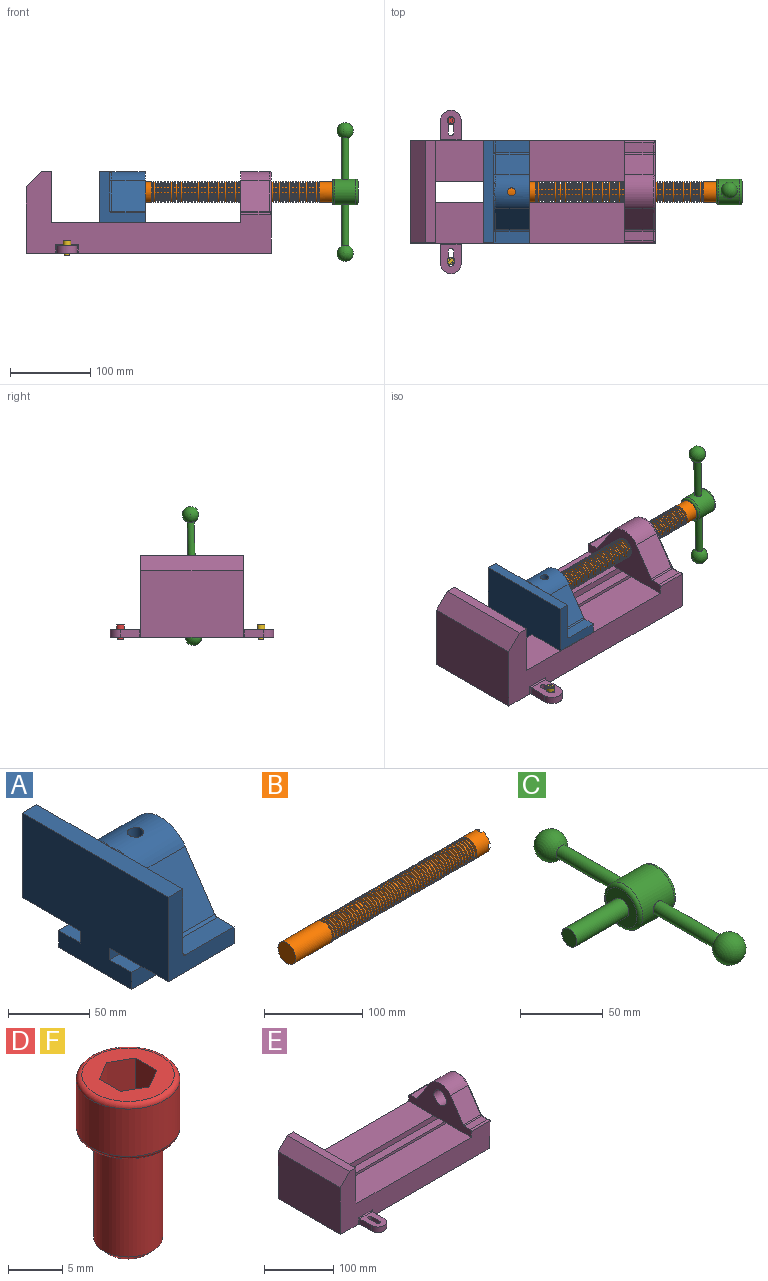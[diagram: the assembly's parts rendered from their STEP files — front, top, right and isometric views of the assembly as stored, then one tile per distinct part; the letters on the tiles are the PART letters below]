
ASSEMBLY  parts=6 mates=6
PART A: 36 faces, bbox 57.2x127x89 mm
  f0: plane 57.15x50.8mm, normal (0,0,-1), area 2903.2mm2, adj f6,f9,f10,f23
  f1: cylinder r=12.7mm len=44.45mm, axis (1,0,0), area 3464.3mm2, adj f6,f15,f16
  f2: plane 41.91x14.52mm, normal (0,0,1), area 608.5mm2, adj f6,f11,f24,f25
  f3: plane 51.86x48.26mm, normal (1,0,0), area 1495.7mm2, adj f8,f10,f31,f33,f35
  f4: plane 51.86x48.26mm, normal (1,0,0), area 1495.7mm2, adj f8,f11,f24,f28,f29
  f5: plane 57.15x50.8mm, normal (0,0,-1), area 2903.2mm2, adj f6,f9,f11,f22
  f6: plane 127x85.09mm, normal (1,0,0), area 5190.6mm2, adj f0,f1,f2,f5,f7,f10,f11,f12
  f7: plane 41.91x14.52mm, normal (0,0,1), area 608.5mm2, adj f6,f10,f30,f31
  f8: plane 127x12.7mm, normal (0,0,1), area 1612.9mm2, adj f3,f4,f9,f10,f11,f26,f34
  f9: plane 127x85.09mm, normal (-1,0,0), area 9096.8mm2, adj f0,f5,f8,f10,f11,f17,f18,f19
  f10: plane 63.5x57.15mm, normal (0,-1,0), area 1372.3mm2, adj f0,f3,f6,f7,f8,f9,f31
  f11: plane 63.5x57.15mm, normal (0,1,0), area 1372.3mm2, adj f2,f4,f5,f6,f8,f9,f24
  f12: plane 41.91x38.43mm, normal (0,-0.83,0.56), area 1939.2mm2, adj f6,f13,f30,f33
  f13: cylinder r=25.4mm len=44.45mm, axis (1,0,0), area 2026.5mm2, adj f6,f12,f14,f16,f26,f28,f34,f35
  f14: plane 41.91x38.43mm, normal (0,0.83,0.56), area 1939.2mm2, adj f6,f13,f25,f29
  f15: plane 25.4x25.4mm, normal (1,0,0), area 506.7mm2, adj f1
  f16: cylinder r=5.08mm len=13.76mm, axis (0,0,1), area 414mm2, adj f1,f13
  f17: plane 57.15x19.05mm, normal (0,0,1), area 1088.7mm2, adj f6,f9,f18,f23
  f18: plane 57.15x12.7mm, normal (0,-1,0), area 725.8mm2, adj f6,f9,f17,f19
  f19: plane 63.5x57.15mm, normal (0,0,-1), area 3629mm2, adj f6,f9,f18,f20
  f20: plane 57.15x12.7mm, normal (0,1,0), area 725.8mm2, adj f6,f9,f19,f21
  f21: plane 57.15x19.05mm, normal (0,0,1), area 1088.7mm2, adj f6,f9,f20,f22
  f22: plane 57.15x8.89mm, normal (0,1,0), area 508.1mm2, adj f5,f6,f9,f21
  f23: plane 57.15x8.89mm, normal (0,-1,0), area 508.1mm2, adj f0,f6,f9,f17
  f24: cylinder r=2.54mm len=14.52mm, axis (0,-1,0), area 57.9mm2, adj f2,f4,f11,f27
  f25: cylinder r=2.54mm len=41.91mm, axis (1,0,0), area 104.3mm2, adj f2,f6,f14,f27
  f26: bspline ~12.24x2.8mm, area 20.9mm2, adj f8,f13,f28
  f27: sphere r=2.54mm, area 6.3mm2, adj f24,f25,f29
  f28: torus R=27.94mm, axis (1,0,0), area 57.8mm2, adj f4,f13,f26,f29
  f29: cylinder r=2.54mm len=39.84mm, axis (0,-0.56,0.83), area 184.6mm2, adj f4,f14,f27,f28
  f30: cylinder r=2.54mm len=41.91mm, axis (1,0,0), area 104.3mm2, adj f6,f7,f12,f32
  f31: cylinder r=2.54mm len=14.52mm, axis (0,-1,0), area 57.9mm2, adj f3,f7,f10,f32
  f32: sphere r=2.54mm, area 6.3mm2, adj f30,f31,f33
  f33: cylinder r=2.54mm len=39.84mm, axis (0,-0.56,-0.83), area 184.6mm2, adj f3,f12,f32,f35
  f34: bspline ~12.24x2.8mm, area 20.9mm2, adj f8,f13,f35
  f35: torus R=27.94mm, axis (1,0,0), area 57.8mm2, adj f3,f13,f33,f34
PART B: 220 faces, bbox 279.4x25.4x25.4 mm
  f0: cylinder r=12.7mm len=25.4mm, axis (-1,0,0), area 1468.2mm2, adj f1,f2,f3,f5,f7,f208,f209,f210
  f1: plane 9.9x9.9mm, normal (1,0,0), area 62.3mm2, adj f0,f4,f213,f216
  f2: plane 9.9x9.9mm, normal (1,0,0), area 62.3mm2, adj f0,f4,f210,f218
  f3: plane 9.9x9.9mm, normal (1,0,0), area 62.3mm2, adj f0,f4,f209,f212
  f4: cylinder r=6.35mm len=25.4mm, axis (1,0,0), area 960.3mm2, adj f1,f2,f3,f5,f6,f208,f209,f210
  f5: plane 9.9x9.9mm, normal (1,0,0), area 62.3mm2, adj f0,f4,f215,f217
  f6: plane 12.7x12.7mm, normal (1,0,0), area 126.7mm2, adj f4
  f7: cone r=12.7mm half-angle=76deg, axis (1,0,0), area 188mm2, adj f0,f9
  f8: cone r=10.16mm half-angle=76deg, axis (-1,0,0), area 188mm2, adj f9,f10
  f9: cylinder r=10.16mm len=20.32mm, axis (1,0,0), area 81.1mm2, adj f7,f8
  f10: cylinder r=12.7mm len=25.4mm, axis (-1,0,0), area 131.7mm2, adj f8,f11
  f11: cone r=12.7mm half-angle=76deg, axis (1,0,0), area 188mm2, adj f10,f13
  f12: cone r=10.16mm half-angle=76deg, axis (-1,0,0), area 188mm2, adj f13,f14
  f13: cylinder r=10.16mm len=20.32mm, axis (1,0,0), area 81.1mm2, adj f11,f12
  f14: cylinder r=12.7mm len=25.4mm, axis (-1,0,0), area 131.7mm2, adj f12,f15
  f15: cone r=12.7mm half-angle=76deg, axis (1,0,0), area 188mm2, adj f14,f17
  f16: cone r=10.16mm half-angle=76deg, axis (-1,0,0), area 188mm2, adj f17,f18
  f17: cylinder r=10.16mm len=20.32mm, axis (1,0,0), area 81.1mm2, adj f15,f16
  f18: cylinder r=12.7mm len=25.4mm, axis (-1,0,0), area 131.7mm2, adj f16,f19
  f19: cone r=12.7mm half-angle=76deg, axis (1,0,0), area 188mm2, adj f18,f21
  f20: cone r=10.16mm half-angle=76deg, axis (-1,0,0), area 188mm2, adj f21,f22
  f21: cylinder r=10.16mm len=20.32mm, axis (1,0,0), area 81.1mm2, adj f19,f20
  f22: cylinder r=12.7mm len=25.4mm, axis (-1,0,0), area 131.7mm2, adj f20,f23
  f23: cone r=12.7mm half-angle=76deg, axis (1,0,0), area 188mm2, adj f22,f25
  f24: cone r=10.16mm half-angle=76deg, axis (-1,0,0), area 188mm2, adj f25,f26
  f25: cylinder r=10.16mm len=20.32mm, axis (1,0,0), area 81.1mm2, adj f23,f24
  f26: cylinder r=12.7mm len=25.4mm, axis (-1,0,0), area 131.7mm2, adj f24,f27
  f27: cone r=12.7mm half-angle=76deg, axis (1,0,0), area 188mm2, adj f26,f29
  f28: cone r=10.16mm half-angle=76deg, axis (-1,0,0), area 188mm2, adj f29,f30
  f29: cylinder r=10.16mm len=20.32mm, axis (1,0,0), area 81.1mm2, adj f27,f28
  f30: cylinder r=12.7mm len=25.4mm, axis (-1,0,0), area 131.7mm2, adj f28,f31
  f31: cone r=12.7mm half-angle=76deg, axis (1,0,0), area 188mm2, adj f30,f33
  f32: cone r=10.16mm half-angle=76deg, axis (-1,0,0), area 188mm2, adj f33,f34
  f33: cylinder r=10.16mm len=20.32mm, axis (1,0,0), area 81.1mm2, adj f31,f32
  f34: cylinder r=12.7mm len=25.4mm, axis (-1,0,0), area 131.7mm2, adj f32,f35
  f35: cone r=12.7mm half-angle=76deg, axis (1,0,0), area 188mm2, adj f34,f37
  f36: cone r=10.16mm half-angle=76deg, axis (-1,0,0), area 188mm2, adj f37,f38
  f37: cylinder r=10.16mm len=20.32mm, axis (1,0,0), area 81.1mm2, adj f35,f36
  f38: cylinder r=12.7mm len=25.4mm, axis (-1,0,0), area 131.7mm2, adj f36,f39
  f39: cone r=12.7mm half-angle=76deg, axis (1,0,0), area 188mm2, adj f38,f41
  f40: cone r=10.16mm half-angle=76deg, axis (-1,0,0), area 188mm2, adj f41,f42
  f41: cylinder r=10.16mm len=20.32mm, axis (1,0,0), area 81.1mm2, adj f39,f40
  f42: cylinder r=12.7mm len=25.4mm, axis (-1,0,0), area 131.7mm2, adj f40,f43
  f43: cone r=12.7mm half-angle=76deg, axis (1,0,0), area 188mm2, adj f42,f45
  f44: cone r=10.16mm half-angle=76deg, axis (-1,0,0), area 188mm2, adj f45,f46
  f45: cylinder r=10.16mm len=20.32mm, axis (1,0,0), area 81.1mm2, adj f43,f44
  f46: cylinder r=12.7mm len=25.4mm, axis (-1,0,0), area 131.7mm2, adj f44,f47
  f47: cone r=12.7mm half-angle=76deg, axis (1,0,0), area 188mm2, adj f46,f49
  f48: cone r=10.16mm half-angle=76deg, axis (-1,0,0), area 188mm2, adj f49,f50
  f49: cylinder r=10.16mm len=20.32mm, axis (1,0,0), area 81.1mm2, adj f47,f48
  f50: cylinder r=12.7mm len=25.4mm, axis (-1,0,0), area 131.7mm2, adj f48,f51
  f51: cone r=12.7mm half-angle=76deg, axis (1,0,0), area 188mm2, adj f50,f53
  f52: cone r=10.16mm half-angle=76deg, axis (-1,0,0), area 188mm2, adj f53,f54
  f53: cylinder r=10.16mm len=20.32mm, axis (1,0,0), area 81.1mm2, adj f51,f52
  f54: cylinder r=12.7mm len=25.4mm, axis (-1,0,0), area 131.7mm2, adj f52,f55
  f55: cone r=12.7mm half-angle=76deg, axis (1,0,0), area 188mm2, adj f54,f57
  f56: cone r=10.16mm half-angle=76deg, axis (-1,0,0), area 188mm2, adj f57,f58
  f57: cylinder r=10.16mm len=20.32mm, axis (1,0,0), area 81.1mm2, adj f55,f56
  f58: cylinder r=12.7mm len=25.4mm, axis (-1,0,0), area 131.7mm2, adj f56,f59
  f59: cone r=12.7mm half-angle=76deg, axis (1,0,0), area 188mm2, adj f58,f61
  f60: cone r=10.16mm half-angle=76deg, axis (-1,0,0), area 188mm2, adj f61,f62
  f61: cylinder r=10.16mm len=20.32mm, axis (1,0,0), area 81.1mm2, adj f59,f60
  f62: cylinder r=12.7mm len=25.4mm, axis (-1,0,0), area 131.7mm2, adj f60,f63
  f63: cone r=12.7mm half-angle=76deg, axis (1,0,0), area 188mm2, adj f62,f65
  f64: cone r=10.16mm half-angle=76deg, axis (-1,0,0), area 188mm2, adj f65,f66
  f65: cylinder r=10.16mm len=20.32mm, axis (1,0,0), area 81.1mm2, adj f63,f64
  f66: cylinder r=12.7mm len=25.4mm, axis (-1,0,0), area 131.7mm2, adj f64,f67
  f67: cone r=12.7mm half-angle=76deg, axis (1,0,0), area 188mm2, adj f66,f69
  f68: cone r=10.16mm half-angle=76deg, axis (-1,0,0), area 188mm2, adj f69,f70
  f69: cylinder r=10.16mm len=20.32mm, axis (1,0,0), area 81.1mm2, adj f67,f68
  f70: cylinder r=12.7mm len=25.4mm, axis (-1,0,0), area 131.7mm2, adj f68,f71
  f71: cone r=12.7mm half-angle=76deg, axis (1,0,0), area 188mm2, adj f70,f73
  f72: cone r=10.16mm half-angle=76deg, axis (-1,0,0), area 188mm2, adj f73,f74
  f73: cylinder r=10.16mm len=20.32mm, axis (1,0,0), area 81.1mm2, adj f71,f72
  f74: cylinder r=12.7mm len=25.4mm, axis (-1,0,0), area 131.7mm2, adj f72,f75
  f75: cone r=12.7mm half-angle=76deg, axis (1,0,0), area 188mm2, adj f74,f77
  f76: cone r=10.16mm half-angle=76deg, axis (-1,0,0), area 188mm2, adj f77,f78
  f77: cylinder r=10.16mm len=20.32mm, axis (1,0,0), area 81.1mm2, adj f75,f76
  f78: cylinder r=12.7mm len=25.4mm, axis (-1,0,0), area 131.7mm2, adj f76,f79
  f79: cone r=12.7mm half-angle=76deg, axis (1,0,0), area 188mm2, adj f78,f81
  f80: cone r=10.16mm half-angle=76deg, axis (-1,0,0), area 188mm2, adj f81,f82
  f81: cylinder r=10.16mm len=20.32mm, axis (1,0,0), area 81.1mm2, adj f79,f80
  f82: cylinder r=12.7mm len=25.4mm, axis (-1,0,0), area 131.7mm2, adj f80,f83
  f83: cone r=12.7mm half-angle=76deg, axis (1,0,0), area 188mm2, adj f82,f85
  f84: cone r=10.16mm half-angle=76deg, axis (-1,0,0), area 188mm2, adj f85,f86
  f85: cylinder r=10.16mm len=20.32mm, axis (1,0,0), area 81.1mm2, adj f83,f84
  f86: cylinder r=12.7mm len=25.4mm, axis (-1,0,0), area 131.7mm2, adj f84,f87
  f87: cone r=12.7mm half-angle=76deg, axis (1,0,0), area 188mm2, adj f86,f89
  f88: cone r=10.16mm half-angle=76deg, axis (-1,0,0), area 188mm2, adj f89,f90
  f89: cylinder r=10.16mm len=20.32mm, axis (1,0,0), area 81.1mm2, adj f87,f88
  f90: cylinder r=12.7mm len=25.4mm, axis (-1,0,0), area 131.7mm2, adj f88,f91
  f91: cone r=12.7mm half-angle=76deg, axis (1,0,0), area 188mm2, adj f90,f93
  f92: cone r=10.16mm half-angle=76deg, axis (-1,0,0), area 188mm2, adj f93,f94
  f93: cylinder r=10.16mm len=20.32mm, axis (1,0,0), area 81.1mm2, adj f91,f92
  f94: cylinder r=12.7mm len=25.4mm, axis (-1,0,0), area 131.7mm2, adj f92,f95
  f95: cone r=12.7mm half-angle=76deg, axis (1,0,0), area 188mm2, adj f94,f97
  f96: cone r=10.16mm half-angle=76deg, axis (-1,0,0), area 188mm2, adj f97,f98
  f97: cylinder r=10.16mm len=20.32mm, axis (1,0,0), area 81.1mm2, adj f95,f96
  f98: cylinder r=12.7mm len=25.4mm, axis (-1,0,0), area 131.7mm2, adj f96,f99
  f99: cone r=12.7mm half-angle=76deg, axis (1,0,0), area 188mm2, adj f98,f101
  f100: cone r=10.16mm half-angle=76deg, axis (-1,0,0), area 188mm2, adj f101,f102
  f101: cylinder r=10.16mm len=20.32mm, axis (1,0,0), area 81.1mm2, adj f99,f100
  f102: cylinder r=12.7mm len=25.4mm, axis (-1,0,0), area 131.7mm2, adj f100,f103
  f103: cone r=12.7mm half-angle=76deg, axis (1,0,0), area 188mm2, adj f102,f105
  f104: cone r=10.16mm half-angle=76deg, axis (-1,0,0), area 188mm2, adj f105,f106
  f105: cylinder r=10.16mm len=20.32mm, axis (1,0,0), area 81.1mm2, adj f103,f104
  f106: cylinder r=12.7mm len=25.4mm, axis (-1,0,0), area 131.7mm2, adj f104,f107
  f107: cone r=12.7mm half-angle=76deg, axis (1,0,0), area 188mm2, adj f106,f109
  f108: cone r=10.16mm half-angle=76deg, axis (-1,0,0), area 188mm2, adj f109,f110
  f109: cylinder r=10.16mm len=20.32mm, axis (1,0,0), area 81.1mm2, adj f107,f108
  f110: cylinder r=12.7mm len=25.4mm, axis (-1,0,0), area 131.7mm2, adj f108,f111
  f111: cone r=12.7mm half-angle=76deg, axis (1,0,0), area 188mm2, adj f110,f113
  f112: cone r=10.16mm half-angle=76deg, axis (-1,0,0), area 188mm2, adj f113,f114
  f113: cylinder r=10.16mm len=20.32mm, axis (1,0,0), area 81.1mm2, adj f111,f112
  f114: cylinder r=12.7mm len=25.4mm, axis (-1,0,0), area 131.7mm2, adj f112,f115
  f115: cone r=12.7mm half-angle=76deg, axis (1,0,0), area 188mm2, adj f114,f117
  f116: cone r=10.16mm half-angle=76deg, axis (-1,0,0), area 188mm2, adj f117,f118
  f117: cylinder r=10.16mm len=20.32mm, axis (1,0,0), area 81.1mm2, adj f115,f116
  f118: cylinder r=12.7mm len=25.4mm, axis (-1,0,0), area 131.7mm2, adj f116,f119
  f119: cone r=12.7mm half-angle=76deg, axis (1,0,0), area 188mm2, adj f118,f121
  f120: cone r=10.16mm half-angle=76deg, axis (-1,0,0), area 188mm2, adj f121,f122
  f121: cylinder r=10.16mm len=20.32mm, axis (1,0,0), area 81.1mm2, adj f119,f120
  f122: cylinder r=12.7mm len=25.4mm, axis (-1,0,0), area 131.7mm2, adj f120,f123
  f123: cone r=12.7mm half-angle=76deg, axis (1,0,0), area 188mm2, adj f122,f125
  f124: cone r=10.16mm half-angle=76deg, axis (-1,0,0), area 188mm2, adj f125,f126
  f125: cylinder r=10.16mm len=20.32mm, axis (1,0,0), area 81.1mm2, adj f123,f124
  f126: cylinder r=12.7mm len=25.4mm, axis (-1,0,0), area 131.7mm2, adj f124,f127
  f127: cone r=12.7mm half-angle=76deg, axis (1,0,0), area 188mm2, adj f126,f129
  f128: cone r=10.16mm half-angle=76deg, axis (-1,0,0), area 188mm2, adj f129,f130
  f129: cylinder r=10.16mm len=20.32mm, axis (1,0,0), area 81.1mm2, adj f127,f128
  f130: cylinder r=12.7mm len=25.4mm, axis (-1,0,0), area 131.7mm2, adj f128,f131
  f131: cone r=12.7mm half-angle=76deg, axis (1,0,0), area 188mm2, adj f130,f133
  f132: cone r=10.16mm half-angle=76deg, axis (-1,0,0), area 188mm2, adj f133,f134
  f133: cylinder r=10.16mm len=20.32mm, axis (1,0,0), area 81.1mm2, adj f131,f132
  f134: cylinder r=12.7mm len=25.4mm, axis (-1,0,0), area 131.7mm2, adj f132,f135
  f135: cone r=12.7mm half-angle=76deg, axis (1,0,0), area 188mm2, adj f134,f137
  f136: cone r=10.16mm half-angle=76deg, axis (-1,0,0), area 188mm2, adj f137,f138
  f137: cylinder r=10.16mm len=20.32mm, axis (1,0,0), area 81.1mm2, adj f135,f136
  f138: cylinder r=12.7mm len=25.4mm, axis (-1,0,0), area 131.7mm2, adj f136,f139
  f139: cone r=12.7mm half-angle=76deg, axis (1,0,0), area 188mm2, adj f138,f141
  f140: cone r=10.16mm half-angle=76deg, axis (-1,0,0), area 188mm2, adj f141,f142
  f141: cylinder r=10.16mm len=20.32mm, axis (1,0,0), area 81.1mm2, adj f139,f140
  f142: cylinder r=12.7mm len=25.4mm, axis (-1,0,0), area 131.7mm2, adj f140,f143
  f143: cone r=12.7mm half-angle=76deg, axis (1,0,0), area 188mm2, adj f142,f145
  f144: cone r=10.16mm half-angle=76deg, axis (-1,0,0), area 188mm2, adj f145,f146
  f145: cylinder r=10.16mm len=20.32mm, axis (1,0,0), area 81.1mm2, adj f143,f144
  f146: cylinder r=12.7mm len=25.4mm, axis (-1,0,0), area 131.7mm2, adj f144,f147
  f147: cone r=12.7mm half-angle=76deg, axis (1,0,0), area 188mm2, adj f146,f149
  f148: cone r=10.16mm half-angle=76deg, axis (-1,0,0), area 188mm2, adj f149,f150
  f149: cylinder r=10.16mm len=20.32mm, axis (1,0,0), area 81.1mm2, adj f147,f148
  f150: cylinder r=12.7mm len=25.4mm, axis (-1,0,0), area 131.7mm2, adj f148,f151
  f151: cone r=12.7mm half-angle=76deg, axis (1,0,0), area 188mm2, adj f150,f153
  f152: cone r=10.16mm half-angle=76deg, axis (-1,0,0), area 188mm2, adj f153,f154
  f153: cylinder r=10.16mm len=20.32mm, axis (1,0,0), area 81.1mm2, adj f151,f152
  f154: cylinder r=12.7mm len=25.4mm, axis (-1,0,0), area 131.7mm2, adj f152,f155
  f155: cone r=12.7mm half-angle=76deg, axis (1,0,0), area 188mm2, adj f154,f157
  f156: cone r=10.16mm half-angle=76deg, axis (-1,0,0), area 188mm2, adj f157,f158
  f157: cylinder r=10.16mm len=20.32mm, axis (1,0,0), area 81.1mm2, adj f155,f156
  f158: cylinder r=12.7mm len=25.4mm, axis (-1,0,0), area 131.7mm2, adj f156,f159
  f159: cone r=12.7mm half-angle=76deg, axis (1,0,0), area 188mm2, adj f158,f161
  f160: cone r=10.16mm half-angle=76deg, axis (-1,0,0), area 188mm2, adj f161,f162
  f161: cylinder r=10.16mm len=20.32mm, axis (1,0,0), area 81.1mm2, adj f159,f160
  f162: cylinder r=12.7mm len=25.4mm, axis (-1,0,0), area 131.7mm2, adj f160,f163
  f163: cone r=12.7mm half-angle=76deg, axis (1,0,0), area 188mm2, adj f162,f165
  f164: cone r=10.16mm half-angle=76deg, axis (-1,0,0), area 188mm2, adj f165,f166
  f165: cylinder r=10.16mm len=20.32mm, axis (1,0,0), area 81.1mm2, adj f163,f164
  f166: cylinder r=12.7mm len=25.4mm, axis (-1,0,0), area 131.7mm2, adj f164,f167
  f167: cone r=12.7mm half-angle=76deg, axis (1,0,0), area 188mm2, adj f166,f169
  f168: cone r=10.16mm half-angle=76deg, axis (-1,0,0), area 188mm2, adj f169,f170
  f169: cylinder r=10.16mm len=20.32mm, axis (1,0,0), area 81.1mm2, adj f167,f168
  f170: cylinder r=12.7mm len=25.4mm, axis (-1,0,0), area 131.7mm2, adj f168,f171
  f171: cone r=12.7mm half-angle=76deg, axis (1,0,0), area 188mm2, adj f170,f173
  f172: cone r=10.16mm half-angle=76deg, axis (-1,0,0), area 188mm2, adj f173,f174
  f173: cylinder r=10.16mm len=20.32mm, axis (1,0,0), area 81.1mm2, adj f171,f172
  f174: cylinder r=12.7mm len=25.4mm, axis (-1,0,0), area 131.7mm2, adj f172,f175
  f175: cone r=12.7mm half-angle=76deg, axis (1,0,0), area 188mm2, adj f174,f177
  f176: cone r=10.16mm half-angle=76deg, axis (-1,0,0), area 188mm2, adj f177,f178
  f177: cylinder r=10.16mm len=20.32mm, axis (1,0,0), area 81.1mm2, adj f175,f176
  f178: cylinder r=12.7mm len=25.4mm, axis (-1,0,0), area 131.7mm2, adj f176,f179
  f179: cone r=12.7mm half-angle=76deg, axis (1,0,0), area 188mm2, adj f178,f181
  f180: cone r=10.16mm half-angle=76deg, axis (-1,0,0), area 188mm2, adj f181,f182
  f181: cylinder r=10.16mm len=20.32mm, axis (1,0,0), area 81.1mm2, adj f179,f180
  f182: cylinder r=12.7mm len=25.4mm, axis (-1,0,0), area 131.7mm2, adj f180,f183
  f183: cone r=12.7mm half-angle=76deg, axis (1,0,0), area 188mm2, adj f182,f185
  f184: cone r=10.16mm half-angle=76deg, axis (-1,0,0), area 188mm2, adj f185,f186
  f185: cylinder r=10.16mm len=20.32mm, axis (1,0,0), area 81.1mm2, adj f183,f184
  f186: cylinder r=12.7mm len=25.4mm, axis (-1,0,0), area 131.7mm2, adj f184,f187
  f187: cone r=12.7mm half-angle=76deg, axis (1,0,0), area 188mm2, adj f186,f189
  f188: cone r=10.16mm half-angle=76deg, axis (-1,0,0), area 188mm2, adj f189,f190
  f189: cylinder r=10.16mm len=20.32mm, axis (1,0,0), area 81.1mm2, adj f187,f188
  f190: cylinder r=12.7mm len=25.4mm, axis (-1,0,0), area 131.7mm2, adj f188,f191
  f191: cone r=12.7mm half-angle=76deg, axis (1,0,0), area 188mm2, adj f190,f193
  f192: cone r=10.16mm half-angle=76deg, axis (-1,0,0), area 188mm2, adj f193,f194
  f193: cylinder r=10.16mm len=20.32mm, axis (1,0,0), area 81.1mm2, adj f191,f192
  f194: cylinder r=12.7mm len=25.4mm, axis (-1,0,0), area 131.7mm2, adj f192,f195
  f195: cone r=12.7mm half-angle=76deg, axis (1,0,0), area 188mm2, adj f194,f197
  f196: cone r=10.16mm half-angle=76deg, axis (-1,0,0), area 188mm2, adj f197,f198
  f197: cylinder r=10.16mm len=20.32mm, axis (1,0,0), area 81.1mm2, adj f195,f196
  f198: cylinder r=12.7mm len=25.4mm, axis (-1,0,0), area 131.7mm2, adj f196,f199
  f199: cone r=12.7mm half-angle=76deg, axis (1,0,0), area 188mm2, adj f198,f201
  f200: cone r=10.16mm half-angle=76deg, axis (-1,0,0), area 188mm2, adj f201,f202
  f201: cylinder r=10.16mm len=20.32mm, axis (1,0,0), area 81.1mm2, adj f199,f200
  f202: cylinder r=12.7mm len=25.4mm, axis (-1,0,0), area 131.7mm2, adj f200,f203
  f203: cone r=12.7mm half-angle=76deg, axis (1,0,0), area 188mm2, adj f202,f205
  f204: cone r=10.16mm half-angle=76deg, axis (-1,0,0), area 188mm2, adj f205,f207
  f205: cylinder r=10.16mm len=20.32mm, axis (1,0,0), area 81.1mm2, adj f203,f204
  f206: plane 25.4x25.4mm, normal (-1,0,0), area 506.7mm2, adj f207
  f207: cylinder r=12.7mm len=52.45mm, axis (-1,0,0), area 4185.4mm2, adj f204,f206
  f208: plane 6.88x5.08mm, normal (1,0,0), area 32.7mm2, adj f0,f4,f209,f210
  f209: plane 6.62x2.54mm, normal (0,-1,0), area 16.8mm2, adj f0,f3,f4,f208
  f210: plane 6.62x2.54mm, normal (0,1,0), area 16.8mm2, adj f0,f2,f4,f208
  f211: plane 6.88x5.08mm, normal (1,0,0), area 32.7mm2, adj f0,f4,f212,f213
  f212: plane 6.62x2.54mm, normal (0,0,1), area 16.8mm2, adj f0,f3,f4,f211
  f213: plane 6.62x2.54mm, normal (0,0,-1), area 16.8mm2, adj f0,f1,f4,f211
  f214: plane 6.88x5.08mm, normal (1,0,0), area 32.7mm2, adj f0,f4,f215,f216
  f215: plane 6.62x2.54mm, normal (0,1,0), area 16.8mm2, adj f0,f4,f5,f214
  f216: plane 6.62x2.54mm, normal (0,-1,0), area 16.8mm2, adj f0,f1,f4,f214
  f217: plane 6.62x2.54mm, normal (0,0,-1), area 16.8mm2, adj f0,f4,f5,f219
  f218: plane 6.62x2.54mm, normal (0,0,1), area 16.8mm2, adj f0,f2,f4,f219
  f219: plane 6.88x5.08mm, normal (1,0,0), area 32.7mm2, adj f0,f4,f217,f218
PART C: 11 faces, bbox 76.2x172.7x34.4 mm
  f0: sphere r=10.16mm, area 1231.8mm2, adj f1
  f1: cylinder r=4.45mm len=51.82mm, axis (0,1,0), area 1438.5mm2, adj f0,f4
  f2: sphere r=10.16mm, area 1231.8mm2, adj f3
  f3: cylinder r=4.45mm len=51.82mm, axis (0,1,0), area 1438.5mm2, adj f2,f4
  f4: cylinder r=15.88mm len=31.75mm, axis (-1,0,0), area 2534.7mm2, adj f1,f3,f9,f10
  f5: cylinder r=6.35mm len=44.45mm, axis (-1,0,0), area 1773.5mm2, adj f6,f8
  f6: plane 12.7x12.7mm, normal (-1,0,0), area 126.7mm2, adj f5
  f7: plane 26.67x26.67mm, normal (1,0,0), area 558.6mm2, adj f10
  f8: plane 26.67x26.67mm, normal (-1,0,0), area 432mm2, adj f5,f9
  f9: torus R=13.33mm, axis (1,0,0), area 374.8mm2, adj f4,f8
  f10: torus R=13.33mm, axis (1,0,0), area 374.8mm2, adj f4,f7
PART D: 15 faces, bbox 10.3x10.3x19.1 mm
  f0: plane 8.51x8.51mm, normal (0,0,1), area 37.2mm2, adj f5,f6,f7,f8,f9,f10,f14
  f1: cylinder r=3.17mm len=11.94mm, axis (0,0,1), area 238.2mm2, adj f4,f12
  f2: plane 4.83x4.83mm, normal (0,0,-1), area 18.3mm2, adj f12
  f3: cylinder r=4.76mm len=9.53mm, axis (0,0,-1), area 159.6mm2, adj f13,f14
  f4: plane 8.51x8.51mm, normal (0,0,-1), area 25.2mm2, adj f1,f13
  f5: plane 4.83x2.38mm, normal (-0.5,-0.87,0), area 13.3mm2, adj f0,f6,f10,f11
  f6: plane 4.83x2.38mm, normal (0.5,-0.87,0), area 13.3mm2, adj f0,f5,f7,f11
  f7: plane 4.83x2.75mm, normal (1,0,0), area 13.3mm2, adj f0,f6,f8,f11
  f8: plane 4.83x2.38mm, normal (0.5,0.87,0), area 13.3mm2, adj f0,f7,f9,f11
  f9: plane 4.83x2.38mm, normal (-0.5,0.87,0), area 13.3mm2, adj f0,f8,f10,f11
  f10: plane 4.83x2.75mm, normal (-1,0,0), area 13.3mm2, adj f0,f5,f9,f11
  f11: plane 5.5x4.76mm, normal (0,0,1), area 19.6mm2, adj f5,f6,f7,f8,f9,f10
  f12: cone r=3.17mm half-angle=45deg, axis (0,0,1), area 18.9mm2, adj f1,f2
  f13: torus R=4.25mm, axis (0,0,1), area 23mm2, adj f3,f4
  f14: torus R=4.25mm, axis (0,0,1), area 23mm2, adj f0,f3
PART E: 61 faces, bbox 304.8x203.2x103.7 mm
  f0: plane 304.8x101.6mm, normal (0,1,0), area 13520.3mm2, adj f3,f4,f5,f6,f7,f8,f9,f16
  f1: plane 304.8x101.6mm, normal (0,-1,0), area 13520.3mm2, adj f2,f3,f5,f6,f7,f8,f9,f16
  f2: plane 234.95x50.8mm, normal (0,0,1), area 11935.5mm2, adj f1,f5,f16,f26
  f3: plane 127x99.06mm, normal (1,0,0), area 7097.5mm2, adj f0,f1,f9,f14,f17,f18,f19,f20
  f4: plane 234.95x50.8mm, normal (0,0,1), area 11935.5mm2, adj f0,f5,f16,f27
  f5: plane 127x101.6mm, normal (1,0,0), area 9516.1mm2, adj f0,f1,f2,f4,f6,f9,f18,f19
  f6: plane 127x12.7mm, normal (0,0,1), area 1612.9mm2, adj f0,f1,f5,f7
  f7: plane 127x19.05mm, normal (-0.71,0,0.71), area 3421.5mm2, adj f0,f1,f6,f8
  f8: plane 127x82.55mm, normal (-1,0,0), area 10483.8mm2, adj f0,f1,f7,f9
  f9: plane 304.8x203.2mm, normal (0,0,-1), area 33298.3mm2, adj f0,f1,f3,f5,f8,f21,f22,f39
  f10: plane 35.56x11.98mm, normal (0,0,1), area 426mm2, adj f16,f28,f29,f30
  f11: plane 38.43x35.56mm, normal (0,0.83,0.56), area 1645.4mm2, adj f12,f16,f29,f32
  f12: cylinder r=25.4mm len=42.19mm, axis (1,0,0), area 1770.2mm2, adj f11,f13,f16,f33
  f13: plane 38.43x35.56mm, normal (0,-0.83,0.56), area 1645.4mm2, adj f12,f16,f34,f35
  f14: cylinder r=12.7mm len=38.1mm, axis (1,0,0), area 3040.2mm2, adj f3,f16
  f15: plane 35.56x11.98mm, normal (0,0,1), area 426mm2, adj f16,f34,f36,f38
  f16: plane 127x63.5mm, normal (-1,0,0), area 4155.5mm2, adj f0,f1,f2,f4,f10,f11,f12,f13
  f17: plane 38.1x25.4mm, normal (0,0,-1), area 967.7mm2, adj f3,f16,f26,f27
  f18: plane 273.05x19.05mm, normal (0,0,-1), area 5201.6mm2, adj f3,f5,f19,f26
  f19: plane 273.05x12.7mm, normal (0,1,0), area 3467.7mm2, adj f3,f5,f18,f20
  f20: plane 273.05x19.05mm, normal (0,0,1), area 5201.6mm2, adj f3,f5,f19,f21
  f21: plane 273.05x16.51mm, normal (0,1,0), area 4508.1mm2, adj f3,f5,f9,f20
  f22: plane 273.05x16.51mm, normal (0,-1,0), area 4508.1mm2, adj f3,f5,f9,f23
  f23: plane 273.05x19.05mm, normal (0,0,1), area 5201.6mm2, adj f3,f5,f22,f24
  f24: plane 273.05x12.7mm, normal (0,-1,0), area 3467.7mm2, adj f3,f5,f23,f25
  f25: plane 273.05x19.05mm, normal (0,0,-1), area 5201.6mm2, adj f3,f5,f24,f27
  f26: plane 273.05x8.89mm, normal (0,1,0), area 2427.4mm2, adj f2,f3,f5,f17,f18
  f27: plane 273.05x8.89mm, normal (0,-1,0), area 2427.4mm2, adj f3,f4,f5,f17,f25
  f28: cylinder r=2.54mm len=38.1mm, axis (1,0,0), area 148.3mm2, adj f0,f10,f16,f30
  f29: cylinder r=2.54mm len=35.56mm, axis (-1,0,0), area 88.5mm2, adj f10,f11,f16,f31
  f30: cylinder r=2.54mm len=14.52mm, axis (0,1,0), area 54.3mm2, adj f3,f10,f28,f31
  f31: torus R=5.08mm, axis (-1,0,0), area 13.5mm2, adj f3,f29,f30,f32
  f32: cylinder r=2.54mm len=39.84mm, axis (0,0.56,-0.83), area 184.6mm2, adj f3,f11,f31,f33
  f33: torus R=22.86mm, axis (-1,0,0), area 191.4mm2, adj f3,f12,f32,f35
  f34: cylinder r=2.54mm len=35.56mm, axis (-1,0,0), area 88.5mm2, adj f13,f15,f16,f37
  f35: cylinder r=2.54mm len=39.84mm, axis (0,0.56,0.83), area 184.6mm2, adj f3,f13,f33,f37
  f36: cylinder r=2.54mm len=38.1mm, axis (-1,0,0), area 148.3mm2, adj f1,f15,f16,f38
  f37: torus R=5.08mm, axis (-1,0,0), area 13.5mm2, adj f3,f34,f35,f38
  f38: cylinder r=2.54mm len=14.52mm, axis (0,1,0), area 54.3mm2, adj f3,f15,f36,f37
  f39: plane 23.88x9.53mm, normal (-1,0,0), area 227.4mm2, adj f9,f45,f46,f60
  f40: plane 23.88x9.53mm, normal (1,0,0), area 227.4mm2, adj f9,f45,f46,f58
  f41: cylinder r=3.3mm len=9.53mm, axis (0,0,-1), area 98.8mm2, adj f9,f42,f44,f46
  f42: plane 15.62x9.53mm, normal (-1,0,0), area 148.8mm2, adj f9,f41,f43,f46
  f43: cylinder r=3.3mm len=9.53mm, axis (0,0,-1), area 98.8mm2, adj f9,f42,f44,f46
  f44: plane 15.62x9.53mm, normal (1,0,0), area 148.8mm2, adj f9,f41,f43,f46
  f45: cylinder r=12.7mm len=25.4mm, axis (0,0,-1), area 380mm2, adj f9,f39,f40,f46
  f46: plane 36.58x25.4mm, normal (0,0,1), area 722.4mm2, adj f39,f40,f41,f42,f43,f44,f45,f59
  f47: plane 23.88x9.53mm, normal (-1,0,0), area 227.4mm2, adj f9,f53,f54,f56
  f48: plane 23.88x9.53mm, normal (1,0,0), area 227.4mm2, adj f9,f53,f54,f55
  f49: cylinder r=3.3mm len=9.53mm, axis (0,0,-1), area 98.8mm2, adj f9,f50,f52,f54
  f50: plane 15.62x9.53mm, normal (-1,0,0), area 148.8mm2, adj f9,f49,f51,f54
  f51: cylinder r=3.3mm len=9.53mm, axis (0,0,-1), area 98.8mm2, adj f9,f50,f52,f54
  f52: plane 15.62x9.53mm, normal (1,0,0), area 148.8mm2, adj f9,f49,f51,f54
  f53: cylinder r=12.7mm len=25.4mm, axis (0,0,-1), area 380mm2, adj f9,f47,f48,f54
  f54: plane 36.58x25.4mm, normal (0,0,1), area 722.4mm2, adj f47,f48,f49,f50,f51,f52,f53,f57
  f55: cylinder r=1.52mm len=11.05mm, axis (0,0,-1), area 24.1mm2, adj f0,f9,f48,f57
  f56: cylinder r=1.52mm len=11.05mm, axis (0,0,1), area 24.1mm2, adj f0,f9,f47,f57
  f57: cylinder r=1.52mm len=28.45mm, axis (1,0,0), area 63.5mm2, adj f0,f54,f55,f56
  f58: cylinder r=1.52mm len=11.05mm, axis (0,0,1), area 24.1mm2, adj f1,f9,f40,f59
  f59: cylinder r=1.52mm len=28.45mm, axis (-1,0,0), area 63.5mm2, adj f1,f46,f58,f60
  f60: cylinder r=1.52mm len=11.05mm, axis (0,0,-1), area 24.1mm2, adj f1,f9,f39,f59
PART F: same geometry as D
PLACE A t=(36.97,-39.69,41.18)mm
PLACE B rot(axis=(-1,0,0),91.4deg) t=(36.97,-115.86,119.26)mm
PLACE C rot(axis=(-1,0,0),91.4deg) t=(15.38,-115.86,119.26)mm
PLACE D t=(-276.55,49.21,50.7)mm
PLACE E t=(-22.55,-39.69,41.18)mm fixed
PLACE F rot(axis=(0,0,-1),77.8deg) t=(-276.55,-125.5,50.7)mm
MATE revolute A.f28 <-> B.f7  axis (1,0,0) through (-223.38,-39.69,117.38)mm
MATE pin_slot D.f1 <-> E.f49  axis (0,0,1) through (-276.55,49.21,50.7)mm
MATE fastened B.f4 <-> C.f5  axis (1,0,0) through (53.48,-39.69,117.38)mm
MATE pin_slot F.f1 <-> E.f41  axis (0,0,1) through (-276.55,-125.5,50.7)mm
MATE cylindrical B.f7 <-> E.f12  axis (1,0,0) through (-82.92,-39.69,117.38)mm
MATE planar A.f0 <-> E.f2  axis (0,0,-1) through (-207.51,-77.79,79.28)mm
